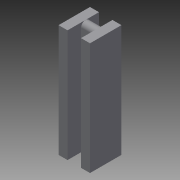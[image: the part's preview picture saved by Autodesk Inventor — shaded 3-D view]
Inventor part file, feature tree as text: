
AUTODESK INVENTOR PART (.ipt)
format: ipt  version: 2015 (Build 190159000, 159)  size: 98,304 bytes
history: native  units: mm
features: fillet x2, extrude x1, sketch x1
ambient origin geometry x8: Origin, YZ Plane, XZ Plane, XY Plane, X Axis, Y Axis, Z Axis, Center Point
bodies: Solid1 (feature_tree)
feature tree (4):
  extrude  "Extrusion1"  Depth=2.0mm
  fillet  "Fillet1"  Radius=3.0mm
  fillet  "Fillet2"  Radius=3.0mm
  sketch  "Sketch1"  dims[d0=2.0mm d1=2.0mm d2=3.0mm d3=3.0mm d4=2.0mm d5=2.0mm d6=25.0mm d7=0.0mm d8=1.0mm d9=1.0mm]
